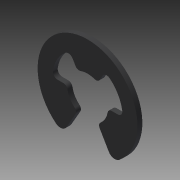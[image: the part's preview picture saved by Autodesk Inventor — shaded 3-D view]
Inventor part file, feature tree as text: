
AUTODESK INVENTOR PART (.ipt)
format: ipt  version: 2014 SP2 (Build 180246200, 246)  size: 128,512 bytes
history: native  units: in
note: dims shown in document units (in); Inventor stores cm internally (conversion verified against a paired STEP export)
features: other x7, extrude x1, sketch x1
ambient origin geometry x8: Origin, YZ Plane, XZ Plane, XY Plane, X Axis, Y Axis, Z Axis, Center Point
bodies: Solid1 (feature_tree)
feature tree (9):
  extrude  "Extrusion1"  [1 undecoded]
  other  "RR_XY"
  other  "RR_YZ"
  other  "RR_ZX"
  other  "RR_X"
  other  "RR_Y"
  other  "RR_Z"
  other  "RR_Center"
  sketch  "Sketch_1"  dims[d0=0.0365in d1=0.0in]
note: 1 required parameter value undecoded (feature->parameter linkage not recoverable at this tier; creation-order binding heuristic only, values carry confidence <= 0.55)
